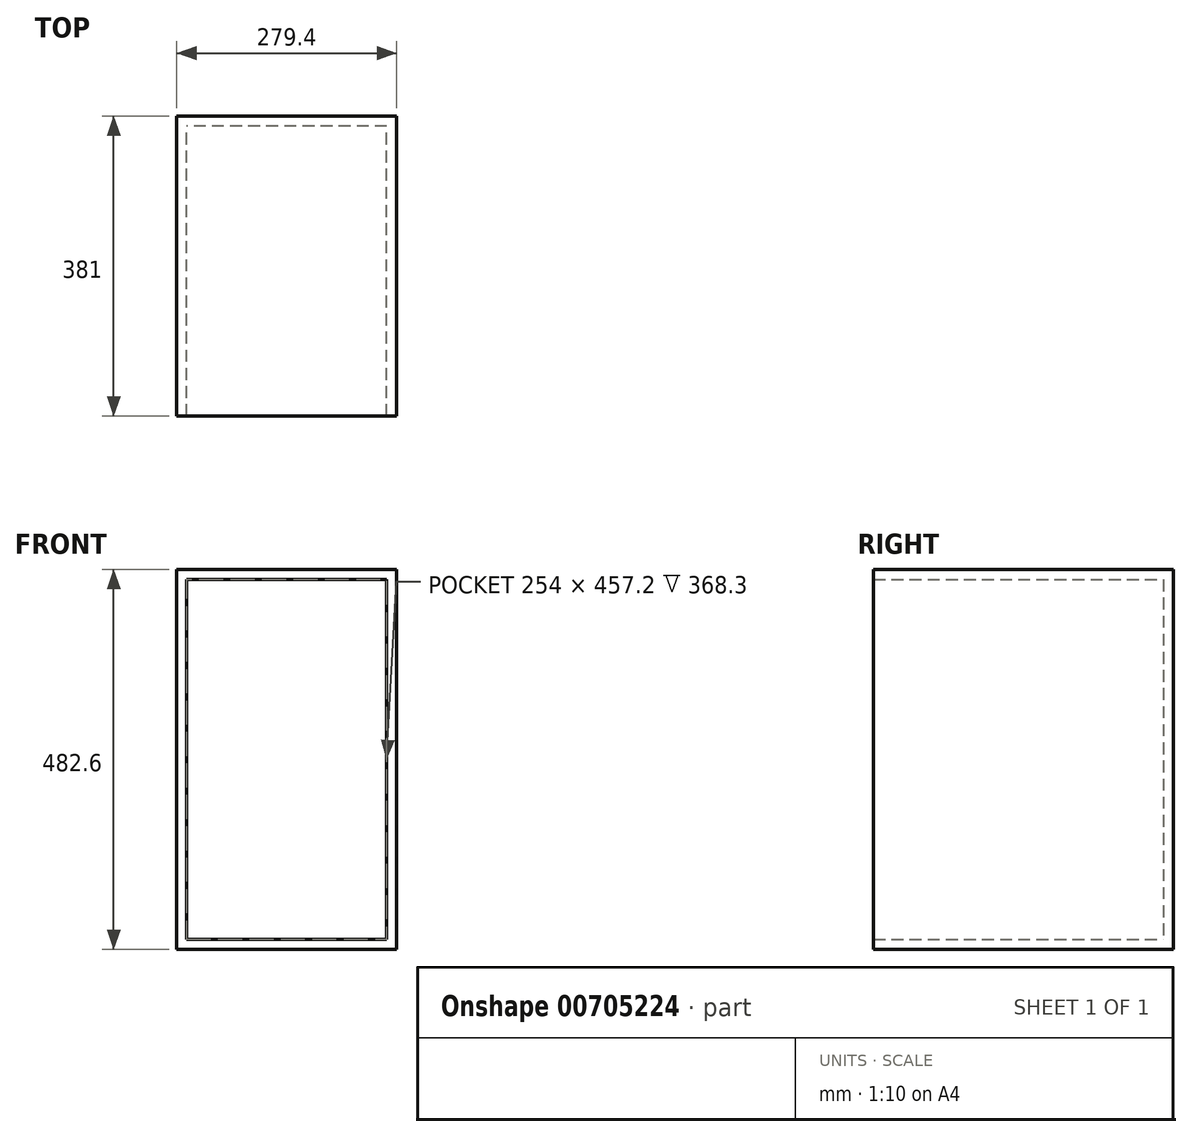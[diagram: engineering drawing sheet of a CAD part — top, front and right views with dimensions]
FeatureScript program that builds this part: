
annotation { "Feature Type Name" : "Feature", "Feature Type Description" : "" }
export const myFeature = defineFeature(function(context is Context, id is Id, definition is map)
    precondition{}
    {
        {
            var Q0;
            Q0=qCreatedBy(makeId("Front.planeOp"),FACE);
            var sketch = newSketch(context, id + "F0", { "sketchPlane" : qUnion([Q0])});
            skLineSegment(sketch, "E0.bottom", {"start": v(139.7, 241.3) * mm, "end": v(-139.7, 241.3) * mm});
            skLineSegment(sketch, "E0.top", {"start": v(139.7, -241.3) * mm, "end": v(-139.7, -241.3) * mm});
            skLineSegment(sketch, "E0.left", {"start": v(139.7, 241.3) * mm, "end": v(139.7, -241.3) * mm});
            skLineSegment(sketch, "E0.right", {"start": v(-139.7, 241.3) * mm, "end": v(-139.7, -241.3) * mm});
            skPoint(sketch, "E0.middle", {"position": v(0, 0) * mm});
            skSolve(sketch);
        }
        {
            var Q0;
            Q0=makeQuery(id+"F0.imprint","IMPRINT",FACE,{"disambiguationData":[TD([[makeQuery(id+"F0.imprint","IMPRINT",EDGE,{"derivedFrom":sQuery(id+"F0.wireOp",EDGE,"E0.bottom")}),1.0]])]});
            var sketch = newSketch(context, id + "F1", { "sketchPlane" : qUnion([Q0])});
            skSolve(sketch);
        }
        {
            var Q0;
            Q0 = qSketchRegion(id + "F1", true);
            var Q1;
            Q1=makeQuery(id+"F0.imprint","IMPRINT",FACE,{"disambiguationData":[TD([[makeQuery(id+"F0.imprint","IMPRINT",EDGE,{"derivedFrom":sQuery(id+"F0.wireOp",EDGE,"E0.bottom")}),1.0]])]});
            extrude(context, id + "F2", {"entities" : qUnion([Q0, Q1]), "depth" : 381 * mm, "offsetDistance" : 25.4 * mm});
        }
        {
            var Q0;
            Q0=makeQuery(id+"F2.opExtrude","CAP_FACE",FACE,{"disambiguationData":[OSD([sQuery(id+"F0.wireOp",EDGE,"E0.bottom"),sQuery(id+"F0.wireOp",EDGE,"E0.top"),sQuery(id+"F0.wireOp",EDGE,"E0.left"),sQuery(id+"F0.wireOp",EDGE,"E0.right")])],"isStart":false});
            shell(context, id + "F3", {"entities" : qUnion([Q0]), "thickness" : 12.7 * mm});
        }
    });
